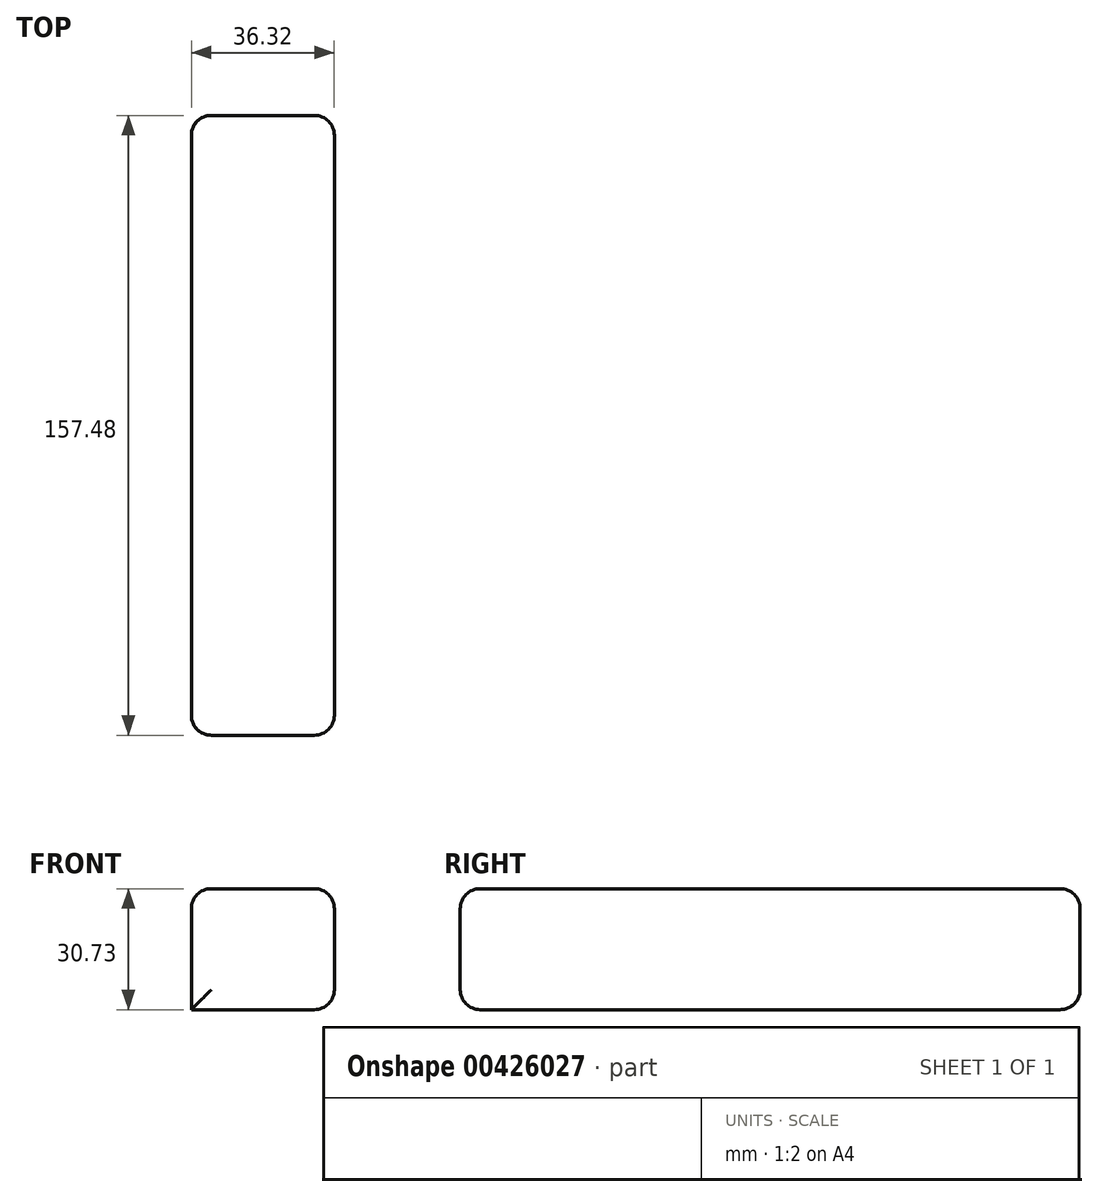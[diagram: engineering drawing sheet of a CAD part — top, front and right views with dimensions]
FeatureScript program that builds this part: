
annotation { "Feature Type Name" : "Feature", "Feature Type Description" : "" }
export const myFeature = defineFeature(function(context is Context, id is Id, definition is map)
    precondition{}
    {
        {
            var Q0;
            Q0=qCreatedBy(makeId("Top.planeOp"),FACE);
            var sketch = newSketch(context, id + "F0", { "sketchPlane" : qUnion([Q0])});
            skLineSegment(sketch, "E0.bottom", {"start": v(-53.7, 93.23) * mm, "end": v(-17.37, 93.23) * mm});
            skLineSegment(sketch, "E0.top", {"start": v(-53.7, -64.25) * mm, "end": v(-17.37, -64.25) * mm});
            skLineSegment(sketch, "E0.left", {"start": v(-53.7, 93.23) * mm, "end": v(-53.7, -64.25) * mm});
            skLineSegment(sketch, "E0.right", {"start": v(-17.37, 93.23) * mm, "end": v(-17.37, -64.25) * mm});
            skSolve(sketch);
        }
        {
            var Q0;
            Q0=makeQuery(id+"F0.imprint","IMPRINT",FACE,{"disambiguationData":[TD([[makeQuery(id+"F0.imprint","IMPRINT",EDGE,{"derivedFrom":sQuery(id+"F0.wireOp",EDGE,"E0.bottom")}),-1.0]])]});
            extrude(context, id + "F1", {"entities" : qUnion([Q0]), "depth" : 30.73 * mm});
        }
        {
            var Q0;
            Q0=makeQuery(id+"F1.opExtrude","SWEPT_FACE",FACE,{"disambiguationData":[OSD([sQuery(id+"F0.wireOp",EDGE,"E0.top")])]});
            var Q1;
            Q1=makeQuery(id+"F1.opExtrude","SWEPT_EDGE",EDGE,{"disambiguationData":[OSD([sQuery(id+"F0.wireOp",EDGE,"E0.bottom"),sQuery(id+"F0.wireOp",EDGE,"E0.right")])]});
            var Q2;
            Q2=makeQuery(id+"F1.opExtrude","SWEPT_EDGE",EDGE,{"disambiguationData":[OSD([sQuery(id+"F0.wireOp",EDGE,"E0.bottom"),sQuery(id+"F0.wireOp",EDGE,"E0.left")])]});
            var Q3;
            Q3=makeQuery(id+"F1.opExtrude","CAP_EDGE",EDGE,{"disambiguationData":[OSD([sQuery(id+"F0.wireOp",EDGE,"E0.bottom")])],"isStart":false});
            var Q4;
            Q4=makeQuery(id+"F1.opExtrude","CAP_EDGE",EDGE,{"disambiguationData":[OSD([sQuery(id+"F0.wireOp",EDGE,"E0.bottom")])],"isStart":true});
            var Q5;
            Q5=makeQuery(id+"F1.opExtrude","CAP_EDGE",EDGE,{"disambiguationData":[OSD([sQuery(id+"F0.wireOp",EDGE,"E0.left")])],"isStart":false});
            var Q6;
            Q6=makeQuery(id+"F1.opExtrude","CAP_EDGE",EDGE,{"disambiguationData":[OSD([sQuery(id+"F0.wireOp",EDGE,"E0.right")])],"isStart":false});
            var Q7;
            Q7=makeQuery(id+"F1.opExtrude","CAP_EDGE",EDGE,{"disambiguationData":[OSD([sQuery(id+"F0.wireOp",EDGE,"E0.right")])],"isStart":true});
            fillet(context, id + "F2", {"entities" : qUnion([Q0, Q1, Q2, Q3, Q4, Q5, Q6, Q7]), "radius" : 5.08 * mm, "tangentPropagation" : true, "allowEdgeOverflow" : false});
        }
    });
